# Revit family: Plumbing_Drainage_hansgrohe_56037USA-RainDrain-Match-Finish-set-show_new
name_source: partatom
category: Plumbing Fixtures
revit_build: Autodesk Revit 2018 (Build: 20170223_1515(x64)
units: mm (PartAtom-declared; Revit-internal decimal feet)

## family parameters
Cut with Voids When Loaded = No
Host = Face
OmniClass Number = 23.31.17.29
OmniClass Title = Shower Drains
Part Type = Normal
Room Calculation Point = No
Round Connector Dimension = Use Diameter
Shared = No

## types (3) — shared parameters
BIMobject category = Drainage
Default Elevation = 48"
Description = RainDrain Match Finish set shower drain 700 with height adjustable frame
Design country = Germany
EAN code = 4059625430569
Edition number = 1
IFC Classification = Pipe Fitting
Manufacturer = Hansgrohe
Manufacturer country = Germany
Manufacturer name = hansgrohe
Masterformat 2014 Code = 22 13 19.13
Masterformat 2014 Description = Sanitary Drains
Material 1 = Hansgrohe - Plastic - Black
Model = 56037USA
OmniClass Code = 23-31 17 29
OmniClass Description = Shower Drains
Product Guid = 6801dd91-5b1c-4f36-9733-4976780fed21
Product SKU = 56037USA
Product data url = https://bimobject.com
Product family = Finish sets shower drains
Product group = RainDrain Match
Product name = 56037USA RainDrain Match Finish set shower drain 700 with height adjustable frame
Product url = https://pro.hansgrohe.com
QR code = https://bimobject.com
UNSPSC Code = 40141719
URL = https://www.hansgrohe.com
Uniclass 2015 Code = Pr_65_52_25
Uniclass 2015 Name = Drainage traps and accessories
Uniformat II Code = D2010
Uniformat II Description = Plumbing Fixtures
Version = 1
Weight Net (Kg) = 2.5

## per-type parameters (varying)
| type | Material |
| 001 Chrome | Hansgrohe - Metal - 001 Chrome |
| 671 Matte Black | Hansgrohe - Metal - 671 Matte Black |
| 801 Stainless Steel Optic | Hansgrohe - Metal - 801 Stainless Steel Optic |

## geometry (parser evidence)
native form markers: Sweep x1
no freeform markers — native parametric forms only
